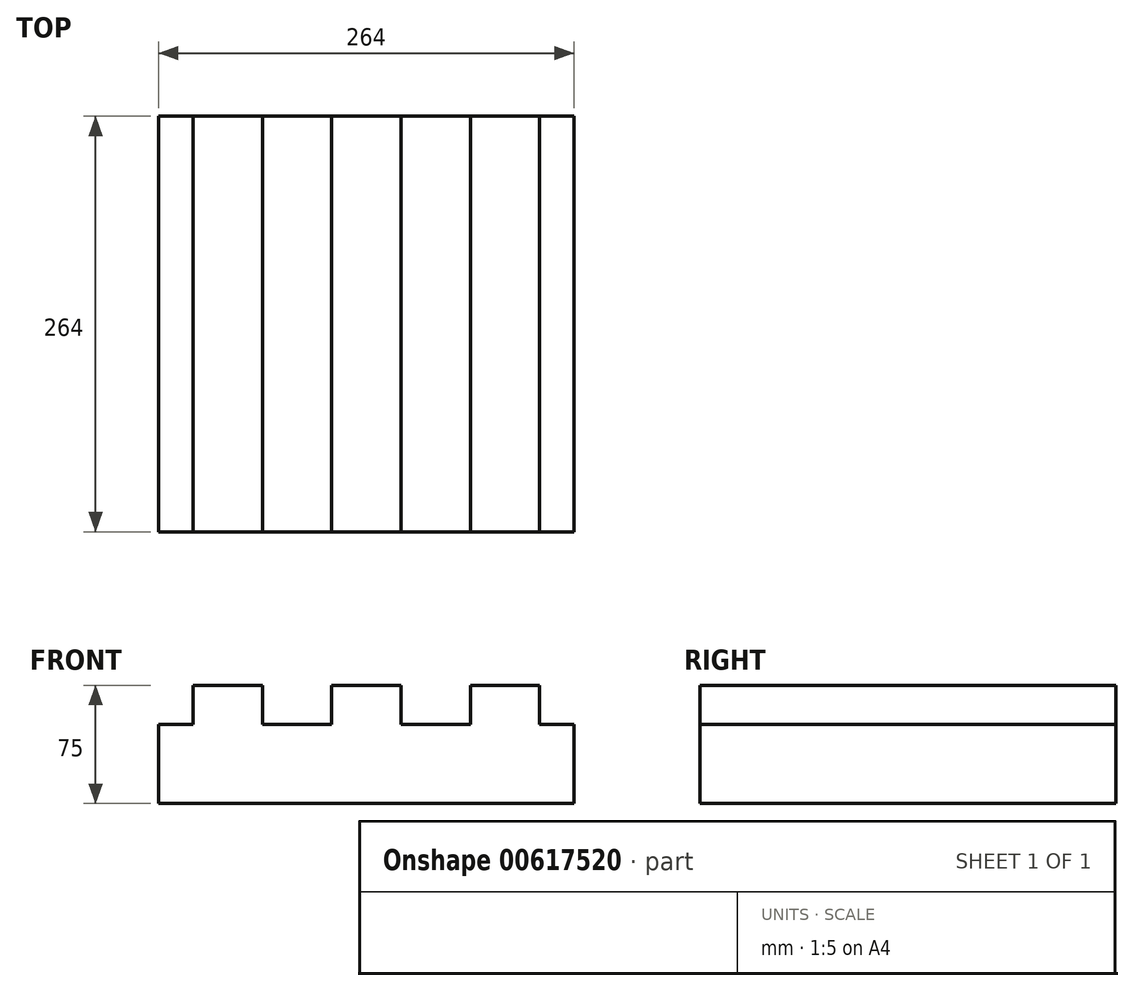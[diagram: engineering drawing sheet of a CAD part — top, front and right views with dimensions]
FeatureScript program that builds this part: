
annotation { "Feature Type Name" : "Feature", "Feature Type Description" : "" }
export const myFeature = defineFeature(function(context is Context, id is Id, definition is map)
    precondition{}
    {
        {
            var Q0;
            Q0=qCreatedBy(makeId("Top.planeOp"),FACE);
            var sketch = newSketch(context, id + "F0", { "sketchPlane" : qUnion([Q0])});
            skLineSegment(sketch, "E0.bottom", {"start": v(22, -22) * mm, "end": v(-22, -22) * mm});
            skLineSegment(sketch, "E0.top", {"start": v(22, 22) * mm, "end": v(-22, 22) * mm});
            skLineSegment(sketch, "E0.left", {"start": v(22, -22) * mm, "end": v(22, 22) * mm});
            skLineSegment(sketch, "E0.right", {"start": v(-22, -22) * mm, "end": v(-22, 22) * mm});
            skPoint(sketch, "E0.middle", {"position": v(0, 0) * mm});
            skLineSegment(sketch, "E1.bottom", {"start": v(-66, -22) * mm, "end": v(-110, -22) * mm});
            skLineSegment(sketch, "E1.top", {"start": v(-66, 22) * mm, "end": v(-110, 22) * mm});
            skLineSegment(sketch, "E1.left", {"start": v(-66, -22) * mm, "end": v(-66, 22) * mm});
            skLineSegment(sketch, "E1.right", {"start": v(-110, -22) * mm, "end": v(-110, 22) * mm});
            skPoint(sketch, "E1.middle", {"position": v(-88, 0) * mm});
            skPoint(sketch, "E1.middle.positionSnap0", {"position": v(-22, 0) * mm});
            skPoint(sketch, "E1.centerSnap0", {"position": v(-22, 0) * mm});
            skLineSegment(sketch, "E2.bottom", {"start": v(22, 66) * mm, "end": v(-22, 66) * mm});
            skLineSegment(sketch, "E2.top", {"start": v(22, 110) * mm, "end": v(-22, 110) * mm});
            skLineSegment(sketch, "E2.left", {"start": v(22, 66) * mm, "end": v(22, 110) * mm});
            skLineSegment(sketch, "E2.right", {"start": v(-22, 66) * mm, "end": v(-22, 110) * mm});
            skLineSegment(sketch, "E3.bottom", {"start": v(-66, 66) * mm, "end": v(-110, 66) * mm});
            skLineSegment(sketch, "E3.top", {"start": v(-66, 110) * mm, "end": v(-110, 110) * mm});
            skLineSegment(sketch, "E3.left", {"start": v(-66, 66) * mm, "end": v(-66, 110) * mm});
            skLineSegment(sketch, "E3.right", {"start": v(-110, 66) * mm, "end": v(-110, 110) * mm});
            skLineSegment(sketch, "E4.bottom", {"start": v(-132, 132) * mm, "end": v(132, 132) * mm});
            skLineSegment(sketch, "E4.top", {"start": v(-132, -132) * mm, "end": v(132, -132) * mm});
            skLineSegment(sketch, "E4.left", {"start": v(-132, 132) * mm, "end": v(-132, -132) * mm});
            skLineSegment(sketch, "E4.right", {"start": v(132, 132) * mm, "end": v(132, -132) * mm});
            skSolve(sketch);
        }
        {
            var Q0;
            Q0=makeQuery(id+"F0.imprint","IMPRINT",FACE,{"disambiguationData":[TD([[makeQuery(id+"F0.imprint","IMPRINT",EDGE,{"derivedFrom":sQuery(id+"F0.wireOp",EDGE,"E1.bottom")}),-1.0]])]});
            var Q1;
            Q1=makeQuery(id+"F0.imprint","IMPRINT",FACE,{"disambiguationData":[TD([[makeQuery(id+"F0.imprint","IMPRINT",EDGE,{"derivedFrom":sQuery(id+"F0.wireOp",EDGE,"E3.bottom")}),-1.0]])]});
            var Q2;
            Q2=makeQuery(id+"F0.imprint","IMPRINT",FACE,{"disambiguationData":[TD([[makeQuery(id+"F0.imprint","IMPRINT",EDGE,{"derivedFrom":sQuery(id+"F0.wireOp",EDGE,"E2.bottom")}),-1.0]])]});
            var Q3;
            Q3=makeQuery(id+"F0.imprint","IMPRINT",FACE,{"disambiguationData":[TD([[makeQuery(id+"F0.imprint","IMPRINT",EDGE,{"derivedFrom":sQuery(id+"F0.wireOp",EDGE,"E0.bottom")}),-1.0]])]});
            extrude(context, id + "F1", {"entities" : qUnion([Q0, Q1, Q2, Q3]), "depth" : 25 * mm, "offsetDistance" : 25 * mm});
        }
        {
            var Q0;
            Q0=makeQuery(id+"F1.opExtrude","SWEPT_BODY",BODY,{"disambiguationData":[OSD([sQuery(id+"F0.wireOp",EDGE,"E1.bottom"),sQuery(id+"F0.wireOp",EDGE,"E1.top"),sQuery(id+"F0.wireOp",EDGE,"E1.left"),sQuery(id+"F0.wireOp",EDGE,"E1.right")])]});
            var Q1;
            Q1=makeQuery(id+"F1.opExtrude","SWEPT_BODY",BODY,{"disambiguationData":[OSD([sQuery(id+"F0.wireOp",EDGE,"E3.bottom"),sQuery(id+"F0.wireOp",EDGE,"E3.top"),sQuery(id+"F0.wireOp",EDGE,"E3.left"),sQuery(id+"F0.wireOp",EDGE,"E3.right")])]});
            var Q2;
            Q2=qCreatedBy(makeId("Right.planeOp"),FACE);
            mirror(context, id + "F2", {"entities" : qUnion([Q0, Q1]), "mirrorPlane" : qUnion([Q2])});
        }
        {
            var Q0;
            Q0=makeQuery(id+"F1.opExtrude","SWEPT_BODY",BODY,{"disambiguationData":[OSD([sQuery(id+"F0.wireOp",EDGE,"E3.bottom"),sQuery(id+"F0.wireOp",EDGE,"E3.top"),sQuery(id+"F0.wireOp",EDGE,"E3.left"),sQuery(id+"F0.wireOp",EDGE,"E3.right")])]});
            var Q1;
            Q1=makeQuery(id+"F1.opExtrude","SWEPT_BODY",BODY,{"disambiguationData":[OSD([sQuery(id+"F0.wireOp",EDGE,"E2.bottom"),sQuery(id+"F0.wireOp",EDGE,"E2.top"),sQuery(id+"F0.wireOp",EDGE,"E2.left"),sQuery(id+"F0.wireOp",EDGE,"E2.right")])]});
            var Q2;
            Q2=makeQuery(id+"F2.opPattern","COPY",BODY,{"derivedFrom":makeQuery(id+"F1.opExtrude","SWEPT_BODY",BODY,{"disambiguationData":[OSD([sQuery(id+"F0.wireOp",EDGE,"E3.bottom"),sQuery(id+"F0.wireOp",EDGE,"E3.top"),sQuery(id+"F0.wireOp",EDGE,"E3.left"),sQuery(id+"F0.wireOp",EDGE,"E3.right")])]}),"instanceName":"1"});
            var Q3;
            Q3=qCreatedBy(makeId("Front.planeOp"),FACE);
            mirror(context, id + "F3", {"entities" : qUnion([Q0, Q1, Q2]), "mirrorPlane" : qUnion([Q3])});
        }
        {
            var Q0;
            Q0=makeQuery(id+"F0.imprint","IMPRINT",FACE,{"disambiguationData":[TD([[makeQuery(id+"F0.imprint","IMPRINT",EDGE,{"derivedFrom":sQuery(id+"F0.wireOp",EDGE,"E0.bottom")}),1.0]])]});
            var Q1;
            Q1=makeQuery(id+"F0.imprint","IMPRINT",FACE,{"disambiguationData":[TD([[makeQuery(id+"F0.imprint","IMPRINT",EDGE,{"derivedFrom":sQuery(id+"F0.wireOp",EDGE,"E1.bottom")}),-1.0]])]});
            var Q2;
            Q2=makeQuery(id+"F0.imprint","IMPRINT",FACE,{"disambiguationData":[TD([[makeQuery(id+"F0.imprint","IMPRINT",EDGE,{"derivedFrom":sQuery(id+"F0.wireOp",EDGE,"E0.bottom")}),-1.0]])]});
            var Q3;
            Q3=makeQuery(id+"F0.imprint","IMPRINT",FACE,{"disambiguationData":[TD([[makeQuery(id+"F0.imprint","IMPRINT",EDGE,{"derivedFrom":sQuery(id+"F0.wireOp",EDGE,"E3.bottom")}),-1.0]])]});
            var Q4;
            Q4=makeQuery(id+"F0.imprint","IMPRINT",FACE,{"disambiguationData":[TD([[makeQuery(id+"F0.imprint","IMPRINT",EDGE,{"derivedFrom":sQuery(id+"F0.wireOp",EDGE,"E2.bottom")}),-1.0]])]});
            extrude(context, id + "F4", {"entities" : qUnion([Q0, Q1, Q2, Q3, Q4]), "oppositeDirection" : true, "depth" : 50 * mm, "offsetDistance" : 25 * mm});
        }
        {
            var Q0;
            Q0=makeQuery(id+"F3.opPattern","COPY",FACE,{"derivedFrom":makeQuery(id+"F1.opExtrude","SWEPT_FACE",FACE,{"disambiguationData":[OSD([sQuery(id+"F0.wireOp",EDGE,"E3.bottom")])]}),"instanceName":"1"});
            var Q1;
            Q1=makeQuery(id+"F1.opExtrude","SWEPT_FACE",FACE,{"disambiguationData":[OSD([sQuery(id+"F0.wireOp",EDGE,"E1.top")])]});
            var Q2;
            Q2=makeQuery(id+"F1.opExtrude","SWEPT_FACE",FACE,{"disambiguationData":[OSD([sQuery(id+"F0.wireOp",EDGE,"E0.top")])]});
            var Q3;
            Q3=makeQuery(id+"F3.opPattern","COPY",FACE,{"derivedFrom":makeQuery(id+"F1.opExtrude","SWEPT_FACE",FACE,{"disambiguationData":[OSD([sQuery(id+"F0.wireOp",EDGE,"E2.bottom")])]}),"instanceName":"1"});
            var Q4;
            Q4=makeQuery(id+"F3.opPattern","COPY",FACE,{"derivedFrom":makeQuery(id+"F2.opPattern","COPY",FACE,{"derivedFrom":makeQuery(id+"F1.opExtrude","SWEPT_FACE",FACE,{"disambiguationData":[OSD([sQuery(id+"F0.wireOp",EDGE,"E3.bottom")])]}),"instanceName":"1"}),"instanceName":"1"});
            var Q5;
            Q5=makeQuery(id+"F2.opPattern","COPY",FACE,{"derivedFrom":makeQuery(id+"F1.opExtrude","SWEPT_FACE",FACE,{"disambiguationData":[OSD([sQuery(id+"F0.wireOp",EDGE,"E1.top")])]}),"instanceName":"1"});
            extrude(context, id + "F5", {"entities" : qUnion([Q0, Q1, Q2, Q3, Q4, Q5]), "operationType" : NewBodyOperationType.ADD, "depth" : 44 * mm, "offsetDistance" : 25 * mm});
        }
        {
            var Q0;
            Q0=makeQuery(id+"F3.opPattern","COPY",FACE,{"derivedFrom":makeQuery(id+"F1.opExtrude","SWEPT_FACE",FACE,{"disambiguationData":[OSD([sQuery(id+"F0.wireOp",EDGE,"E3.top")])]}),"instanceName":"1"});
            var Q1;
            Q1=makeQuery(id+"F3.opPattern","COPY",FACE,{"derivedFrom":makeQuery(id+"F1.opExtrude","SWEPT_FACE",FACE,{"disambiguationData":[OSD([sQuery(id+"F0.wireOp",EDGE,"E2.top")])]}),"instanceName":"1"});
            var Q2;
            Q2=makeQuery(id+"F3.opPattern","COPY",FACE,{"derivedFrom":makeQuery(id+"F2.opPattern","COPY",FACE,{"derivedFrom":makeQuery(id+"F1.opExtrude","SWEPT_FACE",FACE,{"disambiguationData":[OSD([sQuery(id+"F0.wireOp",EDGE,"E3.top")])]}),"instanceName":"1"}),"instanceName":"1"});
            var Q3;
            Q3=makeQuery(id+"F1.opExtrude","SWEPT_FACE",FACE,{"disambiguationData":[OSD([sQuery(id+"F0.wireOp",EDGE,"E3.top")])]});
            var Q4;
            Q4=makeQuery(id+"F1.opExtrude","SWEPT_FACE",FACE,{"disambiguationData":[OSD([sQuery(id+"F0.wireOp",EDGE,"E2.top")])]});
            var Q5;
            Q5=makeQuery(id+"F2.opPattern","COPY",FACE,{"derivedFrom":makeQuery(id+"F1.opExtrude","SWEPT_FACE",FACE,{"disambiguationData":[OSD([sQuery(id+"F0.wireOp",EDGE,"E3.top")])]}),"instanceName":"1"});
            extrude(context, id + "F6", {"entities" : qUnion([Q0, Q1, Q2, Q3, Q4, Q5]), "operationType" : NewBodyOperationType.ADD, "endBound" : BoundingType.SYMMETRIC, "depth" : 44 * mm, "offsetDistance" : 25 * mm});
        }
    });
